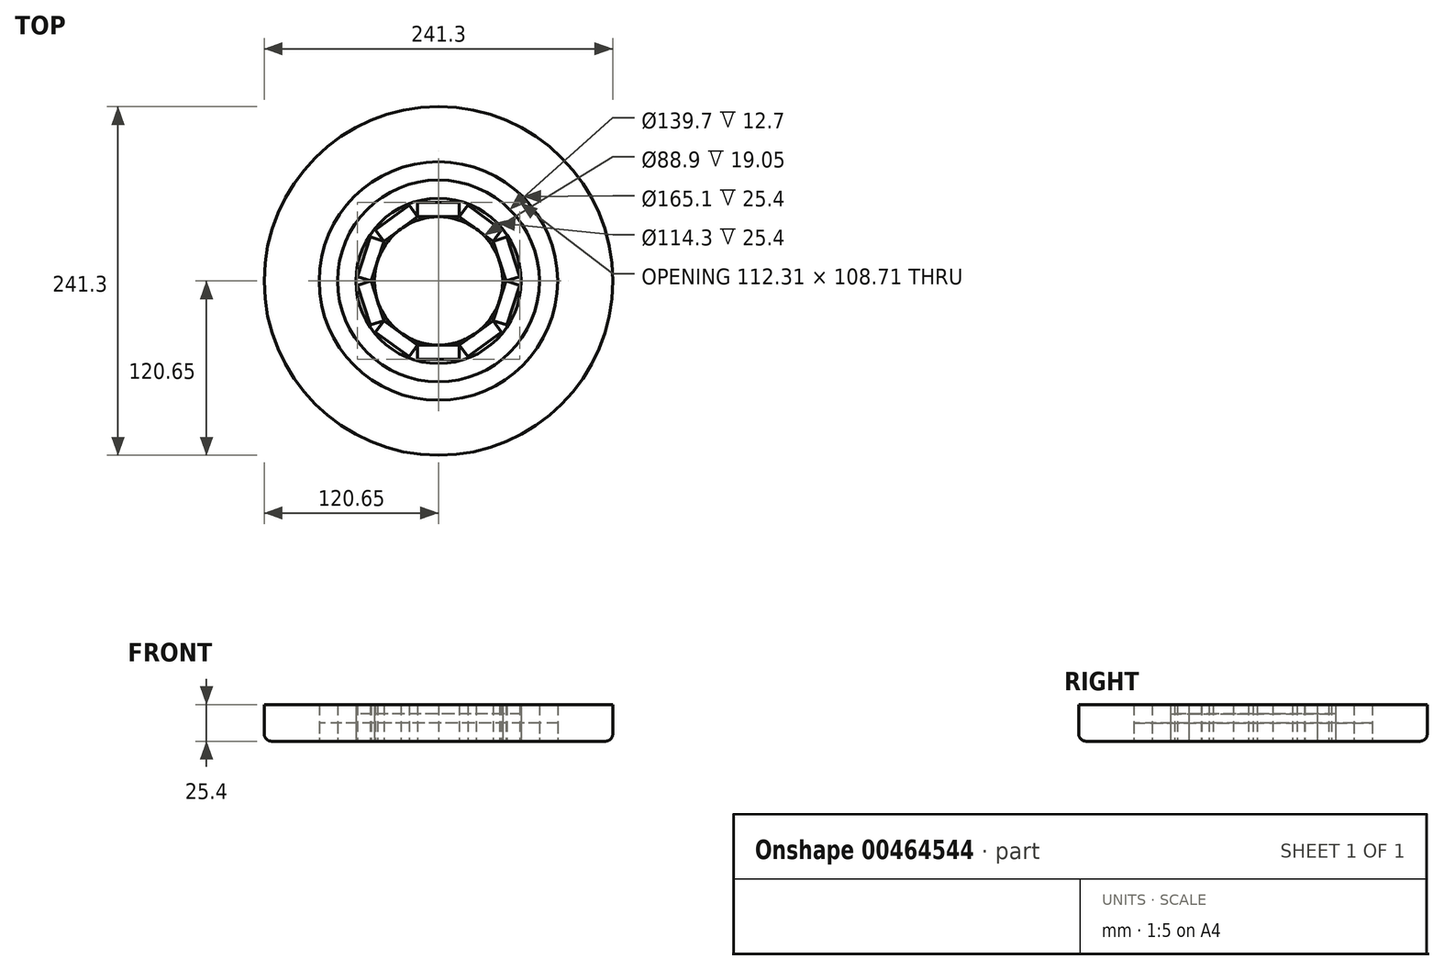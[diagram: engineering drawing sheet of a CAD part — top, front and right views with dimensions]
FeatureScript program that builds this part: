
annotation { "Feature Type Name" : "Feature", "Feature Type Description" : "" }
export const myFeature = defineFeature(function(context is Context, id is Id, definition is map)
    precondition{}
    {
        {
            var Q0;
            Q0=qCreatedBy(makeId("Top.planeOp"),FACE);
            var sketch = newSketch(context, id + "F0", { "sketchPlane" : qUnion([Q0])});
            skCircle(sketch, "E0", {"center": v(0, 0) * mm, "radius": 120.65 * mm});
            skCircle(sketch, "E1", {"center": v(0, 0) * mm, "radius": 44.45 * mm});
            skCircle(sketch, "E2", {"center": v(0, 0) * mm, "radius": 57.15 * mm});
            skCircle(sketch, "E3", {"center": v(0, 0) * mm, "radius": 69.85 * mm});
            skCircle(sketch, "E4", {"center": v(0, 0) * mm, "radius": 82.55 * mm});
            skCircle(sketch, "E5.cCircle", {"center": v(0, 0) * mm, "radius": 44.45 * mm, "construction": true});
            skLineSegment(sketch, "E5.0", {"start": v(-14.44, 44.45) * mm, "end": v(14.44, 44.45) * mm});
            skLineSegment(sketch, "E5.1", {"start": v(14.44, 44.45) * mm, "end": v(37.81, 27.47) * mm});
            skLineSegment(sketch, "E5.2", {"start": v(37.81, 27.47) * mm, "end": v(46.74, 0) * mm});
            skLineSegment(sketch, "E5.3", {"start": v(46.74, 0) * mm, "end": v(37.81, -27.47) * mm});
            skLineSegment(sketch, "E5.4", {"start": v(37.81, -27.47) * mm, "end": v(14.44, -44.45) * mm});
            skLineSegment(sketch, "E5.5", {"start": v(14.44, -44.45) * mm, "end": v(-14.44, -44.45) * mm});
            skLineSegment(sketch, "E5.6", {"start": v(-14.44, -44.45) * mm, "end": v(-37.81, -27.47) * mm});
            skLineSegment(sketch, "E5.7", {"start": v(-37.81, -27.47) * mm, "end": v(-46.74, 0) * mm});
            skLineSegment(sketch, "E5.8", {"start": v(-46.74, 0) * mm, "end": v(-37.81, 27.47) * mm});
            skLineSegment(sketch, "E5.9", {"start": v(-37.81, 27.47) * mm, "end": v(-14.44, 44.45) * mm});
            skPoint(sketch, "E5.0.midPoint", {"position": v(0, 44.45) * mm});
            skCircle(sketch, "E6.cCircle", {"center": v(0, 0) * mm, "radius": 57.15 * mm, "construction": true});
            skLineSegment(sketch, "E6.0", {"start": v(-17.66, 54.35) * mm, "end": v(17.66, 54.35) * mm});
            skLineSegment(sketch, "E6.1", {"start": v(17.66, 54.35) * mm, "end": v(46.24, 33.6) * mm});
            skLineSegment(sketch, "E6.2", {"start": v(46.24, 33.6) * mm, "end": v(57.15, 0) * mm});
            skLineSegment(sketch, "E6.3", {"start": v(57.15, 0) * mm, "end": v(46.24, -33.6) * mm});
            skLineSegment(sketch, "E6.4", {"start": v(46.24, -33.6) * mm, "end": v(17.66, -54.35) * mm});
            skLineSegment(sketch, "E6.5", {"start": v(17.66, -54.35) * mm, "end": v(-17.66, -54.35) * mm});
            skLineSegment(sketch, "E6.6", {"start": v(-17.66, -54.35) * mm, "end": v(-46.24, -33.6) * mm});
            skLineSegment(sketch, "E6.7", {"start": v(-46.24, -33.6) * mm, "end": v(-57.15, 0) * mm});
            skLineSegment(sketch, "E6.8", {"start": v(-57.15, 0) * mm, "end": v(-46.24, 33.6) * mm});
            skLineSegment(sketch, "E6.9", {"start": v(-46.24, 33.6) * mm, "end": v(-17.66, 54.35) * mm});
            skLineSegment(sketch, "E7", {"start": v(-14.44, 44.45) * mm, "end": v(-14.44, 54.35) * mm});
            skLineSegment(sketch, "E8", {"start": v(-14.44, 44.45) * mm, "end": v(-20.26, 52.46) * mm});
            skLineSegment(sketch, "E9", {"start": v(-37.81, 27.47) * mm, "end": v(-43.63, 35.48) * mm});
            skLineSegment(sketch, "E10", {"start": v(-37.81, 27.47) * mm, "end": v(-47.23, 30.53) * mm});
            skLineSegment(sketch, "E11", {"start": v(14.44, 44.45) * mm, "end": v(14.44, 54.35) * mm});
            skLineSegment(sketch, "E12", {"start": v(14.44, 44.45) * mm, "end": v(20.26, 52.46) * mm});
            skLineSegment(sketch, "E13", {"start": v(37.81, 27.47) * mm, "end": v(43.63, 35.48) * mm});
            skLineSegment(sketch, "E14", {"start": v(37.81, 27.47) * mm, "end": v(47.23, 30.53) * mm});
            skLineSegment(sketch, "E15", {"start": v(46.74, 0) * mm, "end": v(56.16, 3.06) * mm});
            skLineSegment(sketch, "E16", {"start": v(46.74, 0) * mm, "end": v(56.16, -3.06) * mm});
            skLineSegment(sketch, "E17", {"start": v(37.81, -27.47) * mm, "end": v(47.23, -30.53) * mm});
            skLineSegment(sketch, "E18", {"start": v(37.81, -27.47) * mm, "end": v(43.63, -35.48) * mm});
            skLineSegment(sketch, "E19", {"start": v(14.44, -44.45) * mm, "end": v(20.26, -52.46) * mm});
            skLineSegment(sketch, "E20", {"start": v(14.44, -44.45) * mm, "end": v(14.44, -54.35) * mm});
            skLineSegment(sketch, "E21", {"start": v(-14.44, -44.45) * mm, "end": v(-14.44, -54.35) * mm});
            skLineSegment(sketch, "E22", {"start": v(-14.44, -44.45) * mm, "end": v(-20.26, -52.46) * mm});
            skLineSegment(sketch, "E23", {"start": v(-37.81, -27.47) * mm, "end": v(-43.63, -35.48) * mm});
            skLineSegment(sketch, "E24", {"start": v(-37.81, -27.47) * mm, "end": v(-47.23, -30.53) * mm});
            skLineSegment(sketch, "E25", {"start": v(-46.74, 0) * mm, "end": v(-56.16, 3.06) * mm});
            skLineSegment(sketch, "E26", {"start": v(-46.74, 0) * mm, "end": v(-56.16, -3.06) * mm});
            skCircle(sketch, "E27.cCircle", {"center": v(0, 0) * mm, "radius": 69.85 * mm, "construction": true});
            skPoint(sketch, "E27.cCircle.perimeterSnap0", {"position": v(0, -54.35) * mm});
            skPoint(sketch, "E27.0.midPoint.positionSnap0", {"position": v(0, -54.35) * mm});
            skLineSegment(sketch, "E28.0", {"start": v(22.7, -69.85) * mm, "end": v(-22.7, -69.85) * mm});
            skLineSegment(sketch, "E28.1", {"start": v(-22.7, -69.85) * mm, "end": v(-59.42, -43.17) * mm});
            skLineSegment(sketch, "E28.2", {"start": v(-59.42, -43.17) * mm, "end": v(-73.44, 0) * mm});
            skLineSegment(sketch, "E28.3", {"start": v(-73.44, 0) * mm, "end": v(-59.42, 43.17) * mm});
            skLineSegment(sketch, "E28.4", {"start": v(-59.42, 43.17) * mm, "end": v(-22.7, 69.85) * mm});
            skLineSegment(sketch, "E28.5", {"start": v(-22.7, 69.85) * mm, "end": v(22.7, 69.85) * mm});
            skLineSegment(sketch, "E28.6", {"start": v(22.7, 69.85) * mm, "end": v(59.42, 43.17) * mm});
            skLineSegment(sketch, "E28.7", {"start": v(59.42, 43.17) * mm, "end": v(73.44, 0) * mm});
            skLineSegment(sketch, "E28.8", {"start": v(73.44, 0) * mm, "end": v(59.42, -43.17) * mm});
            skLineSegment(sketch, "E28.9", {"start": v(59.42, -43.17) * mm, "end": v(22.7, -69.85) * mm});
            skPoint(sketch, "E28.0.midPoint", {"position": v(0, -69.85) * mm});
            skCircle(sketch, "E29.cCircle", {"center": v(0, 0) * mm, "radius": 82.55 * mm, "construction": true});
            skLineSegment(sketch, "E29.0", {"start": v(25.5, -78.5) * mm, "end": v(-25.5, -78.5) * mm});
            skLineSegment(sketch, "E29.1", {"start": v(-25.5, -78.5) * mm, "end": v(-66.78, -48.52) * mm});
            skLineSegment(sketch, "E29.2", {"start": v(-66.78, -48.52) * mm, "end": v(-82.55, 0) * mm});
            skLineSegment(sketch, "E29.3", {"start": v(-82.55, 0) * mm, "end": v(-66.78, 48.52) * mm});
            skLineSegment(sketch, "E29.4", {"start": v(-66.78, 48.52) * mm, "end": v(-25.5, 78.5) * mm});
            skLineSegment(sketch, "E29.5", {"start": v(-25.5, 78.5) * mm, "end": v(25.5, 78.5) * mm});
            skLineSegment(sketch, "E29.6", {"start": v(25.5, 78.5) * mm, "end": v(66.78, 48.52) * mm});
            skLineSegment(sketch, "E29.7", {"start": v(66.78, 48.52) * mm, "end": v(82.55, 0) * mm});
            skLineSegment(sketch, "E29.8", {"start": v(82.55, 0) * mm, "end": v(66.78, -48.52) * mm});
            skLineSegment(sketch, "E29.9", {"start": v(66.78, -48.52) * mm, "end": v(25.5, -78.5) * mm});
            skLineSegment(sketch, "E30", {"start": v(-22.7, -69.85) * mm, "end": v(-25.5, -78.5) * mm});
            skLineSegment(sketch, "E31", {"start": v(-59.42, -43.17) * mm, "end": v(-66.78, -48.52) * mm});
            skLineSegment(sketch, "E32", {"start": v(-59.42, -43.17) * mm, "end": v(-64.5, -50.18) * mm});
            skLineSegment(sketch, "E33", {"start": v(-22.7, -69.85) * mm, "end": v(-27.79, -76.86) * mm});
            skLineSegment(sketch, "E34", {"start": v(-22.7, -69.85) * mm, "end": v(-22.7, -78.5) * mm});
            skSolve(sketch);
        }
        {
            var Q0;
            Q0=makeQuery(id+"F0.imprint","IMPRINT",FACE,{"disambiguationData":[TD([[makeQuery(id+"F0.imprint","IMPRINT",EDGE,{"derivedFrom":sQuery(id+"F0.wireOp",EDGE,"E0")}),1.0]])]});
            var Q1;
            Q1=makeQuery(id+"F0.imprint","IMPRINT",FACE,{"disambiguationData":[TD([[makeQuery(id+"F0.imprint","IMPRINT",EDGE,{"derivedFrom":sQuery(id+"F0.wireOp",EDGE,"E2")}),-1.0]])]});
            var Q2;
            Q2=makeQuery(id+"F0.imprint","IMPRINT",FACE,{"disambiguationData":[TD([[makeQuery(id+"F0.imprint","IMPRINT",EDGE,{"derivedFrom":sQuery(id+"F0.wireOp",EDGE,"E1")}),1.0]])]});
            extrude(context, id + "F1", {"entities" : qUnion([Q0, Q1, Q2]), "depth" : 25.4 * mm});
        }
        {
            var Q0;
            Q0=qCreatedBy(makeId("Top.planeOp"),FACE);
            var sketch = newSketch(context, id + "F2", { "sketchPlane" : qUnion([Q0])});
            skCircle(sketch, "E35", {"center": v(0, 0) * mm, "radius": 82.55 * mm});
            skCircle(sketch, "E36", {"center": v(0, 0) * mm, "radius": 69.85 * mm});
            skCircle(sketch, "E37", {"center": v(0, 0) * mm, "radius": 57.15 * mm});
            skCircle(sketch, "E38", {"center": v(0, 0) * mm, "radius": 44.45 * mm});
            skSolve(sketch);
        }
        {
            var Q0;
            Q0=makeQuery(id+"F2.imprint","IMPRINT",FACE,{"disambiguationData":[TD([[makeQuery(id+"F2.imprint","IMPRINT",EDGE,{"derivedFrom":sQuery(id+"F2.wireOp",EDGE,"E35")}),1.0]])]});
            extrude(context, id + "F3", {"entities" : qUnion([Q0]), "depth" : 12.7 * mm});
        }
        {
            var Q0;
            Q0=makeQuery(id+"F2.imprint","IMPRINT",FACE,{"disambiguationData":[TD([[makeQuery(id+"F2.imprint","IMPRINT",EDGE,{"derivedFrom":sQuery(id+"F2.wireOp",EDGE,"E37")}),1.0]])]});
            extrude(context, id + "F4", {"entities" : qUnion([Q0]), "depth" : 19.05 * mm});
        }
        {
            var Q0;
            Q0=makeQuery(id+"F1.opExtrude","CAP_EDGE",EDGE,{"disambiguationData":[OSD([sQuery(id+"F0.wireOp",EDGE,"E0")])],"isStart":true});
            fillet(context, id + "F5", {"entities" : qUnion([Q0]), "radius" : 5.08 * mm, "tangentPropagation" : true, "allowEdgeOverflow" : false});
        }
        {
            var Q0;
            {var subQ3=sQuery(id+"F0.wireOp",EDGE,"E7");Q0=makeQuery(id+"F0.imprint","IMPRINT",FACE,{"disambiguationData":[TD([[makeQuery(id+"F0.imprint","IMPRINT",EDGE,{"derivedFrom":subQ3}),1.0]])]});}
            var Q1;
            {var subQ0=sQuery(id+"F0.wireOp",EDGE,"E6.0");var subQ4=makeQuery(id+"F0.imprint","INTERSECT",VERTEX,{"derivedFrom":[subQ0,sQuery(id+"F0.wireOp",EDGE,"E7")]});Q1=makeQuery(id+"F0.imprint","IMPRINT",FACE,{"disambiguationData":[TD([[makeQuery(id+"F0.imprint","IMPRINT",EDGE,{"disambiguationData":[TD([[subQ4,-1.0]])],"derivedFrom":subQ0}),1.0]])]});}
            var Q2;
            {var subQ0=sQuery(id+"F0.wireOp",EDGE,"E6.9");var subQ5=makeQuery(id+"F0.imprint","INTERSECT",VERTEX,{"derivedFrom":[subQ0,sQuery(id+"F0.wireOp",EDGE,"E8")]});Q2=makeQuery(id+"F0.imprint","IMPRINT",FACE,{"disambiguationData":[TD([[makeQuery(id+"F0.imprint","IMPRINT",EDGE,{"disambiguationData":[TD([[subQ5,1.0]])],"derivedFrom":subQ0}),1.0]])]});}
            var Q3;
            {var subQ0=sQuery(id+"F0.wireOp",EDGE,"E5.0");var subQ1=sQuery(id+"F0.wireOp",EDGE,"E1");var subQ2=makeQuery(id+"F0.imprint","INTERSECT",VERTEX,{"derivedFrom":[subQ1,subQ0]});Q3=makeQuery(id+"F0.imprint","IMPRINT",FACE,{"disambiguationData":[TD([[makeQuery(id+"F0.imprint","IMPRINT",EDGE,{"disambiguationData":[TD([[subQ2,-1.0]])],"derivedFrom":subQ1}),-1.0]])]});}
            var Q4;
            {var subQ3=sQuery(id+"F0.wireOp",EDGE,"E11");Q4=makeQuery(id+"F0.imprint","IMPRINT",FACE,{"disambiguationData":[TD([[makeQuery(id+"F0.imprint","IMPRINT",EDGE,{"derivedFrom":subQ3}),-1.0]])]});}
            var Q5;
            {var subQ0=sQuery(id+"F0.wireOp",EDGE,"E5.1");var subQ1=sQuery(id+"F0.wireOp",EDGE,"E1");var subQ2=makeQuery(id+"F0.imprint","INTERSECT",VERTEX,{"derivedFrom":[subQ1,subQ0]});Q5=makeQuery(id+"F0.imprint","IMPRINT",FACE,{"disambiguationData":[TD([[makeQuery(id+"F0.imprint","IMPRINT",EDGE,{"disambiguationData":[TD([[subQ2,-1.0]])],"derivedFrom":subQ1}),-1.0]])]});}
            var Q6;
            {var subQ0=sQuery(id+"F0.wireOp",EDGE,"E6.1");var subQ4=makeQuery(id+"F0.imprint","INTERSECT",VERTEX,{"derivedFrom":[subQ0,sQuery(id+"F0.wireOp",EDGE,"E12")]});Q6=makeQuery(id+"F0.imprint","IMPRINT",FACE,{"disambiguationData":[TD([[makeQuery(id+"F0.imprint","IMPRINT",EDGE,{"disambiguationData":[TD([[subQ4,-1.0]])],"derivedFrom":subQ0}),1.0]])]});}
            var Q7;
            {var subQ0=sQuery(id+"F0.wireOp",EDGE,"E5.1");var subQ1=sQuery(id+"F0.wireOp",EDGE,"E1");var subQ2=makeQuery(id+"F0.imprint","INTERSECT",VERTEX,{"derivedFrom":[subQ1,subQ0]});Q7=makeQuery(id+"F0.imprint","IMPRINT",FACE,{"disambiguationData":[TD([[makeQuery(id+"F0.imprint","IMPRINT",EDGE,{"disambiguationData":[TD([[subQ2,1.0]])],"derivedFrom":subQ1}),-1.0]])]});}
            var Q8;
            {var subQ3=sQuery(id+"F0.wireOp",EDGE,"E13");Q8=makeQuery(id+"F0.imprint","IMPRINT",FACE,{"disambiguationData":[TD([[makeQuery(id+"F0.imprint","IMPRINT",EDGE,{"derivedFrom":subQ3}),-1.0]])]});}
            var Q9;
            {var subQ0=sQuery(id+"F0.wireOp",EDGE,"E6.2");var subQ5=makeQuery(id+"F0.imprint","INTERSECT",VERTEX,{"derivedFrom":[subQ0,sQuery(id+"F0.wireOp",EDGE,"E14")]});Q9=makeQuery(id+"F0.imprint","IMPRINT",FACE,{"disambiguationData":[TD([[makeQuery(id+"F0.imprint","IMPRINT",EDGE,{"disambiguationData":[TD([[subQ5,-1.0]])],"derivedFrom":subQ0}),1.0]])]});}
            var Q10;
            {var subQ0=sQuery(id+"F0.wireOp",EDGE,"E5.2");var subQ1=sQuery(id+"F0.wireOp",EDGE,"E1");var subQ2=makeQuery(id+"F0.imprint","INTERSECT",VERTEX,{"derivedFrom":[subQ1,subQ0]});Q10=makeQuery(id+"F0.imprint","IMPRINT",FACE,{"disambiguationData":[TD([[makeQuery(id+"F0.imprint","IMPRINT",EDGE,{"disambiguationData":[TD([[subQ2,1.0]])],"derivedFrom":subQ1}),-1.0]])]});}
            var Q11;
            {var subQ3=sQuery(id+"F0.wireOp",EDGE,"E15");Q11=makeQuery(id+"F0.imprint","IMPRINT",FACE,{"disambiguationData":[TD([[makeQuery(id+"F0.imprint","IMPRINT",EDGE,{"derivedFrom":subQ3}),-1.0]])]});}
            var Q12;
            {var subQ0=sQuery(id+"F0.wireOp",EDGE,"E6.3");var subQ4=makeQuery(id+"F0.imprint","INTERSECT",VERTEX,{"derivedFrom":[subQ0,sQuery(id+"F0.wireOp",EDGE,"E16")]});Q12=makeQuery(id+"F0.imprint","IMPRINT",FACE,{"disambiguationData":[TD([[makeQuery(id+"F0.imprint","IMPRINT",EDGE,{"disambiguationData":[TD([[subQ4,-1.0]])],"derivedFrom":subQ0}),1.0]])]});}
            var Q13;
            {var subQ0=sQuery(id+"F0.wireOp",EDGE,"E5.4");var subQ1=sQuery(id+"F0.wireOp",EDGE,"E1");var subQ2=makeQuery(id+"F0.imprint","INTERSECT",VERTEX,{"derivedFrom":[subQ1,subQ0]});Q13=makeQuery(id+"F0.imprint","IMPRINT",FACE,{"disambiguationData":[TD([[makeQuery(id+"F0.imprint","IMPRINT",EDGE,{"disambiguationData":[TD([[subQ2,-1.0]])],"derivedFrom":subQ1}),-1.0]])]});}
            var Q14;
            {var subQ3=sQuery(id+"F0.wireOp",EDGE,"E17");Q14=makeQuery(id+"F0.imprint","IMPRINT",FACE,{"disambiguationData":[TD([[makeQuery(id+"F0.imprint","IMPRINT",EDGE,{"derivedFrom":subQ3}),-1.0]])]});}
            var Q15;
            {var subQ0=sQuery(id+"F0.wireOp",EDGE,"E6.4");var subQ4=makeQuery(id+"F0.imprint","INTERSECT",VERTEX,{"derivedFrom":[subQ0,sQuery(id+"F0.wireOp",EDGE,"E18")]});Q15=makeQuery(id+"F0.imprint","IMPRINT",FACE,{"disambiguationData":[TD([[makeQuery(id+"F0.imprint","IMPRINT",EDGE,{"disambiguationData":[TD([[subQ4,-1.0]])],"derivedFrom":subQ0}),1.0]])]});}
            var Q16;
            {var subQ0=sQuery(id+"F0.wireOp",EDGE,"E6.5");var subQ4=makeQuery(id+"F0.imprint","INTERSECT",VERTEX,{"derivedFrom":[subQ0,sQuery(id+"F0.wireOp",EDGE,"E20")]});Q16=makeQuery(id+"F0.imprint","IMPRINT",FACE,{"disambiguationData":[TD([[makeQuery(id+"F0.imprint","IMPRINT",EDGE,{"disambiguationData":[TD([[subQ4,-1.0]])],"derivedFrom":subQ0}),1.0]])]});}
            var Q17;
            {var subQ3=sQuery(id+"F0.wireOp",EDGE,"E19");Q17=makeQuery(id+"F0.imprint","IMPRINT",FACE,{"disambiguationData":[TD([[makeQuery(id+"F0.imprint","IMPRINT",EDGE,{"derivedFrom":subQ3}),-1.0]])]});}
            var Q18;
            {var subQ0=sQuery(id+"F0.wireOp",EDGE,"E5.5");var subQ1=sQuery(id+"F0.wireOp",EDGE,"E1");var subQ2=makeQuery(id+"F0.imprint","INTERSECT",VERTEX,{"derivedFrom":[subQ1,subQ0]});Q18=makeQuery(id+"F0.imprint","IMPRINT",FACE,{"disambiguationData":[TD([[makeQuery(id+"F0.imprint","IMPRINT",EDGE,{"disambiguationData":[TD([[subQ2,-1.0]])],"derivedFrom":subQ1}),-1.0]])]});}
            var Q19;
            {var subQ0=sQuery(id+"F0.wireOp",EDGE,"E5.6");var subQ1=sQuery(id+"F0.wireOp",EDGE,"E1");var subQ2=makeQuery(id+"F0.imprint","INTERSECT",VERTEX,{"derivedFrom":[subQ1,subQ0]});Q19=makeQuery(id+"F0.imprint","IMPRINT",FACE,{"disambiguationData":[TD([[makeQuery(id+"F0.imprint","IMPRINT",EDGE,{"disambiguationData":[TD([[subQ2,-1.0]])],"derivedFrom":subQ1}),-1.0]])]});}
            var Q20;
            {var subQ3=sQuery(id+"F0.wireOp",EDGE,"E21");Q20=makeQuery(id+"F0.imprint","IMPRINT",FACE,{"disambiguationData":[TD([[makeQuery(id+"F0.imprint","IMPRINT",EDGE,{"derivedFrom":subQ3}),-1.0]])]});}
            var Q21;
            {var subQ0=sQuery(id+"F0.wireOp",EDGE,"E6.6");var subQ4=makeQuery(id+"F0.imprint","INTERSECT",VERTEX,{"derivedFrom":[subQ0,sQuery(id+"F0.wireOp",EDGE,"E22")]});Q21=makeQuery(id+"F0.imprint","IMPRINT",FACE,{"disambiguationData":[TD([[makeQuery(id+"F0.imprint","IMPRINT",EDGE,{"disambiguationData":[TD([[subQ4,-1.0]])],"derivedFrom":subQ0}),1.0]])]});}
            var Q22;
            {var subQ3=sQuery(id+"F0.wireOp",EDGE,"E23");Q22=makeQuery(id+"F0.imprint","IMPRINT",FACE,{"disambiguationData":[TD([[makeQuery(id+"F0.imprint","IMPRINT",EDGE,{"derivedFrom":subQ3}),-1.0]])]});}
            var Q23;
            {var subQ0=sQuery(id+"F0.wireOp",EDGE,"E5.7");var subQ1=sQuery(id+"F0.wireOp",EDGE,"E1");var subQ2=makeQuery(id+"F0.imprint","INTERSECT",VERTEX,{"derivedFrom":[subQ1,subQ0]});Q23=makeQuery(id+"F0.imprint","IMPRINT",FACE,{"disambiguationData":[TD([[makeQuery(id+"F0.imprint","IMPRINT",EDGE,{"disambiguationData":[TD([[subQ2,-1.0]])],"derivedFrom":subQ1}),-1.0]])]});}
            var Q24;
            {var subQ0=sQuery(id+"F0.wireOp",EDGE,"E6.7");var subQ5=makeQuery(id+"F0.imprint","INTERSECT",VERTEX,{"derivedFrom":[subQ0,sQuery(id+"F0.wireOp",EDGE,"E24")]});Q24=makeQuery(id+"F0.imprint","IMPRINT",FACE,{"disambiguationData":[TD([[makeQuery(id+"F0.imprint","IMPRINT",EDGE,{"disambiguationData":[TD([[subQ5,-1.0]])],"derivedFrom":subQ0}),1.0]])]});}
            var Q25;
            {var subQ0=sQuery(id+"F0.wireOp",EDGE,"E5.8");var subQ1=sQuery(id+"F0.wireOp",EDGE,"E1");var subQ2=makeQuery(id+"F0.imprint","INTERSECT",VERTEX,{"derivedFrom":[subQ1,subQ0]});Q25=makeQuery(id+"F0.imprint","IMPRINT",FACE,{"disambiguationData":[TD([[makeQuery(id+"F0.imprint","IMPRINT",EDGE,{"disambiguationData":[TD([[subQ2,-1.0]])],"derivedFrom":subQ1}),-1.0]])]});}
            var Q26;
            {var subQ4=sQuery(id+"F0.wireOp",EDGE,"E25");Q26=makeQuery(id+"F0.imprint","IMPRINT",FACE,{"disambiguationData":[TD([[makeQuery(id+"F0.imprint","IMPRINT",EDGE,{"derivedFrom":subQ4}),1.0]])]});}
            var Q27;
            {var subQ0=sQuery(id+"F0.wireOp",EDGE,"E6.8");var subQ5=makeQuery(id+"F0.imprint","INTERSECT",VERTEX,{"derivedFrom":[subQ0,sQuery(id+"F0.wireOp",EDGE,"E10")]});Q27=makeQuery(id+"F0.imprint","IMPRINT",FACE,{"disambiguationData":[TD([[makeQuery(id+"F0.imprint","IMPRINT",EDGE,{"disambiguationData":[TD([[subQ5,1.0]])],"derivedFrom":subQ0}),1.0]])]});}
            var Q28;
            {var subQ0=sQuery(id+"F0.wireOp",EDGE,"E5.9");var subQ1=sQuery(id+"F0.wireOp",EDGE,"E1");var subQ2=makeQuery(id+"F0.imprint","INTERSECT",VERTEX,{"derivedFrom":[subQ1,subQ0]});Q28=makeQuery(id+"F0.imprint","IMPRINT",FACE,{"disambiguationData":[TD([[makeQuery(id+"F0.imprint","IMPRINT",EDGE,{"disambiguationData":[TD([[subQ2,-1.0]])],"derivedFrom":subQ1}),-1.0]])]});}
            var Q29;
            {var subQ4=sQuery(id+"F0.wireOp",EDGE,"E9");Q29=makeQuery(id+"F0.imprint","IMPRINT",FACE,{"disambiguationData":[TD([[makeQuery(id+"F0.imprint","IMPRINT",EDGE,{"derivedFrom":subQ4}),1.0]])]});}
            extrude(context, id + "F6", {"entities" : qUnion([Q0, Q1, Q2, Q3, Q4, Q5, Q6, Q7, Q8, Q9, Q10, Q11, Q12, Q13, Q14, Q15, Q16, Q17, Q18, Q19, Q20, Q21, Q22, Q23, Q24, Q25, Q26, Q27, Q28, Q29]), "depth" : 25.4 * mm});
        }
    });
